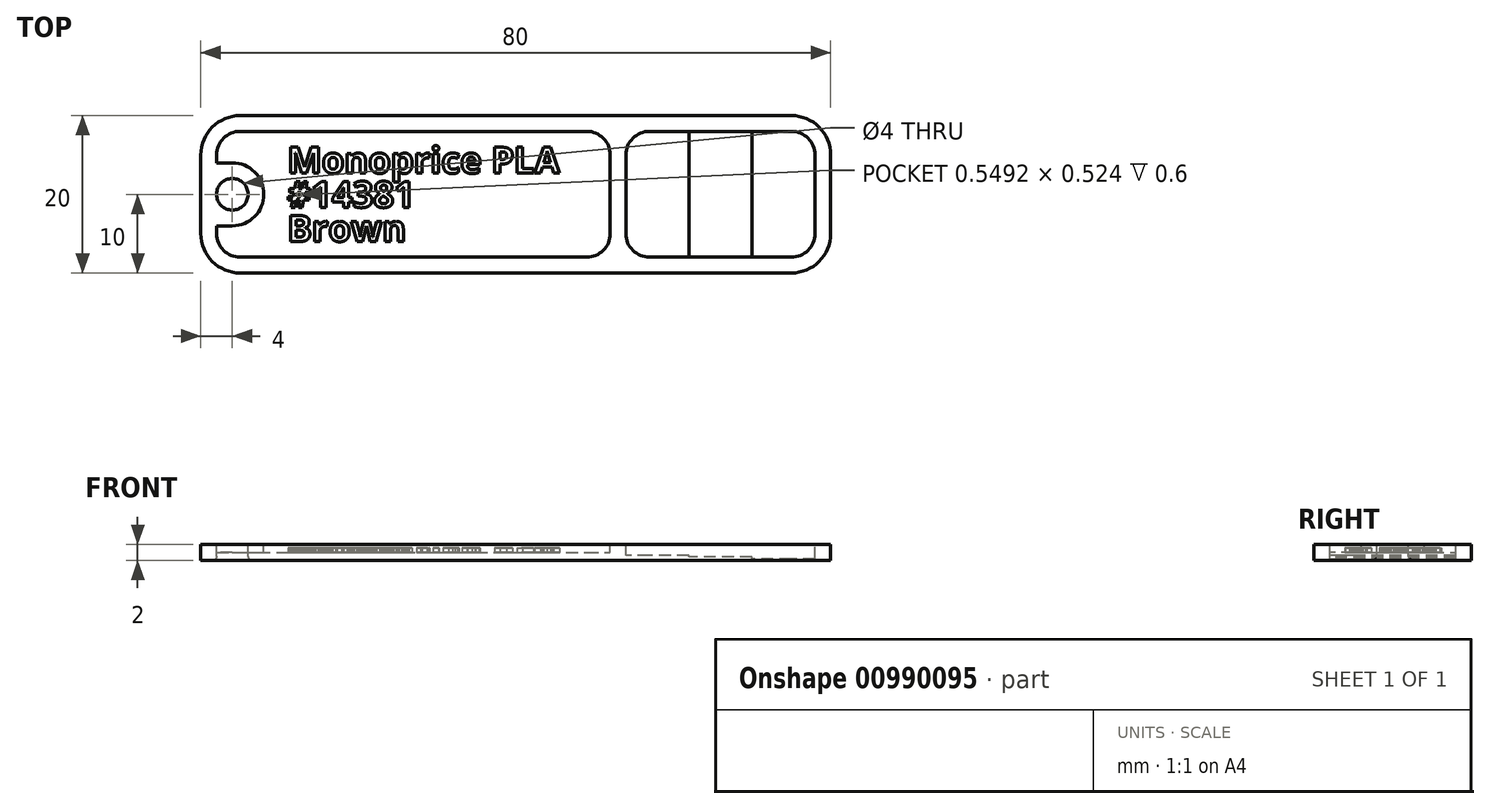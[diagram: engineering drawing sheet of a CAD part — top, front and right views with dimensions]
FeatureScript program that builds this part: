
annotation { "Feature Type Name" : "Feature", "Feature Type Description" : "" }
export const myFeature = defineFeature(function(context is Context, id is Id, definition is map)
    precondition{}
    {
        {
            var Q0;
            Q0=qCreatedBy(makeId("Top.planeOp"),FACE);
            var sketch = newSketch(context, id + "F0", { "sketchPlane" : qUnion([Q0])});
            skLineSegment(sketch, "E0.bottom", {"start": v(35, 10) * mm, "end": v(-35, 10) * mm});
            skLineSegment(sketch, "E0.top", {"start": v(35, -10) * mm, "end": v(-35, -10) * mm});
            skLineSegment(sketch, "E0.left", {"start": v(40, 5) * mm, "end": v(40, -5) * mm});
            skLineSegment(sketch, "E0.right", {"start": v(-40, 5) * mm, "end": v(-40, -5) * mm});
            skPoint(sketch, "E0.middle", {"position": v(0, 0) * mm});
            skPoint(sketch, "E1.visualSharp", {"position": v(-40, 10) * mm});
            skArc(sketch, "E1.filletArc", {"start": v(-35, 10) * mm, "mid": v(-38.54, 8.54) * mm, "end": v(-40, 5) * mm});
            skPoint(sketch, "E2.visualSharp", {"position": v(40, 10) * mm});
            skArc(sketch, "E2.filletArc", {"start": v(40, 5) * mm, "mid": v(38.54, 8.54) * mm, "end": v(35, 10) * mm});
            skPoint(sketch, "E3.visualSharp", {"position": v(40, -10) * mm});
            skArc(sketch, "E3.filletArc", {"start": v(35, -10) * mm, "mid": v(38.54, -8.54) * mm, "end": v(40, -5) * mm});
            skPoint(sketch, "E4.visualSharp", {"position": v(-40, -10) * mm});
            skArc(sketch, "E4.filletArc", {"start": v(-40, -5) * mm, "mid": v(-38.54, -8.54) * mm, "end": v(-35, -10) * mm});
            skSolve(sketch);
        }
        {
            var Q0;
            Q0=qSketchRegion(id+"F0",true);
            extrude(context, id + "F1", {"entities" : qUnion([Q0]), "offsetDistance" : 25 * mm, "depth" : 2 * mm});
        }
        {
            var Q0;
            Q0=makeQuery(id+"F1.opExtrude","CAP_FACE",FACE,{"disambiguationData":[OSD([sQuery(id+"F0.wireOp",EDGE,"E0.bottom"),sQuery(id+"F0.wireOp",EDGE,"E0.top"),sQuery(id+"F0.wireOp",EDGE,"E0.left"),sQuery(id+"F0.wireOp",EDGE,"E0.right"),sQuery(id+"F0.wireOp",EDGE,"E1.filletArc"),sQuery(id+"F0.wireOp",EDGE,"E2.filletArc"),sQuery(id+"F0.wireOp",EDGE,"E3.filletArc"),sQuery(id+"F0.wireOp",EDGE,"E4.filletArc")])],"isStart":false});
            var sketch = newSketch(context, id + "F2", { "sketchPlane" : qUnion([Q0])});
            skLineSegment(sketch, "E5.0", {"start": v(38, -5) * mm, "end": v(38, 5) * mm});
            skArc(sketch, "E5.1", {"start": v(35, -8) * mm, "mid": v(37.12, -7.12) * mm, "end": v(38, -5) * mm});
            skArc(sketch, "E5.2", {"start": v(38, 5) * mm, "mid": v(37.12, 7.12) * mm, "end": v(35, 8) * mm});
            skLineSegment(sketch, "E5.3", {"start": v(-35, -8) * mm, "end": v(9, -8) * mm});
            skLineSegment(sketch, "E5.4", {"start": v(35, 8) * mm, "end": v(17, 8) * mm});
            skArc(sketch, "E5.5", {"start": v(-35, 8) * mm, "mid": v(-37.12, 7.12) * mm, "end": v(-38, 5) * mm});
            skArc(sketch, "E5.7", {"start": v(-38, -5) * mm, "mid": v(-37.12, -7.12) * mm, "end": v(-35, -8) * mm});
            skCircle(sketch, "E6", {"center": v(-36, 0) * mm, "radius": 2 * mm, "construction": true});
            skArc(sketch, "E7.0", {"start": v(-36, -4) * mm, "mid": v(-32, 0) * mm, "end": v(-36, 4) * mm});
            skLineSegment(sketch, "E8", {"start": v(-38, -5) * mm, "end": v(-38, -4) * mm});
            skLineSegment(sketch, "E9", {"start": v(-36, 4) * mm, "end": v(-38, 4) * mm});
            skLineSegment(sketch, "E10", {"start": v(-36, -4) * mm, "end": v(-38, -4) * mm});
            skLineSegment(sketch, "E11.trimOffspring", {"start": v(-38, 4) * mm, "end": v(-38, 5) * mm});
            skArc(sketch, "E12", {"start": v(17, 8) * mm, "mid": v(14.88, 7.12) * mm, "end": v(14, 5) * mm});
            skArc(sketch, "E13", {"start": v(14, -5) * mm, "mid": v(14.88, -7.12) * mm, "end": v(17, -8) * mm});
            skLineSegment(sketch, "E14", {"start": v(14, -5) * mm, "end": v(14, 5) * mm});
            skArc(sketch, "E15", {"start": v(12, 5) * mm, "mid": v(11.12, 7.12) * mm, "end": v(9, 8) * mm});
            skArc(sketch, "E16", {"start": v(12, -5) * mm, "mid": v(11.12, -7.12) * mm, "end": v(9, -8) * mm});
            skLineSegment(sketch, "E17", {"start": v(12, -5) * mm, "end": v(12, 5) * mm});
            skLineSegment(sketch, "E18.trimOffspring", {"start": v(9, 8) * mm, "end": v(-35, 8) * mm});
            skLineSegment(sketch, "E19.trimOffspring", {"start": v(17, -8) * mm, "end": v(35, -8) * mm});
            skSolve(sketch);
        }
        {
            var Q0;
            Q0=qSketchRegion(id+"F2",true);
            extrude(context, id + "F3", {"entities" : qUnion([Q0]), "operationType" : NewBodyOperationType.REMOVE, "oppositeDirection" : true, "offsetDistance" : 25 * mm, "depth" : 1 * mm});
        }
        {
            var Q0;
            Q0=makeQuery(id+"F1.opExtrude","CAP_FACE",FACE,{"disambiguationData":[OSD([sQuery(id+"F0.wireOp",EDGE,"E0.bottom"),sQuery(id+"F0.wireOp",EDGE,"E0.top"),sQuery(id+"F0.wireOp",EDGE,"E0.left"),sQuery(id+"F0.wireOp",EDGE,"E0.right"),sQuery(id+"F0.wireOp",EDGE,"E1.filletArc"),sQuery(id+"F0.wireOp",EDGE,"E2.filletArc"),sQuery(id+"F0.wireOp",EDGE,"E3.filletArc"),sQuery(id+"F0.wireOp",EDGE,"E4.filletArc")])],"isStart":false});
            var sketch = newSketch(context, id + "F4", { "sketchPlane" : qUnion([Q0])});
            skCircle(sketch, "E20.0", {"center": v(-36, 0) * mm, "radius": 2 * mm});
            skSolve(sketch);
        }
        {
            var Q0;
            Q0=qSketchRegion(id+"F4",true);
            extrude(context, id + "F5", {"entities" : qUnion([Q0]), "operationType" : NewBodyOperationType.REMOVE, "endBound" : BoundingType.THROUGH_ALL, "oppositeDirection" : true, "depth" : 25 * mm});
        }
        {
            var Q0;
            Q0=makeQuery(id+"F5.boolean.opBoolean","COPY",EDGE,{"derivedFrom":makeQuery(id+"F5.opExtrude","CAP_EDGE",EDGE,{"disambiguationData":[OSD([sQuery(id+"F4.wireOp",EDGE,"E20.0")])],"isStart":true})});
            var Q1;
            Q1=makeQuery(id+"F5.boolean.opBoolean","INTERSECT",EDGE,{"derivedFrom":[makeQuery(id+"F1.opExtrude","CAP_FACE",FACE,{"disambiguationData":[OSD([sQuery(id+"F0.wireOp",EDGE,"E0.bottom"),sQuery(id+"F0.wireOp",EDGE,"E0.top"),sQuery(id+"F0.wireOp",EDGE,"E0.left"),sQuery(id+"F0.wireOp",EDGE,"E0.right"),sQuery(id+"F0.wireOp",EDGE,"E1.filletArc"),sQuery(id+"F0.wireOp",EDGE,"E2.filletArc"),sQuery(id+"F0.wireOp",EDGE,"E3.filletArc"),sQuery(id+"F0.wireOp",EDGE,"E4.filletArc")])],"isStart":true}),makeQuery(id+"F5.opExtrude","SWEPT_FACE",FACE,{"disambiguationData":[OSD([sQuery(id+"F4.wireOp",EDGE,"E20.0")])]})]});
            fillet(context, id + "F6", {"entities" : qUnion([Q0, Q1]), "radius" : .5 * mm, "tangentPropagation" : true, "allowEdgeOverflow" : false});
        }
        {
            var Q0;
            Q0=makeQuery(id+"F3.boolean.opBoolean","COPY",FACE,{"derivedFrom":makeQuery(id+"F3.opExtrude","CAP_FACE",FACE,{"disambiguationData":[OSD([sQuery(id+"F2.wireOp",EDGE,"E5.0"),sQuery(id+"F2.wireOp",EDGE,"E5.1"),sQuery(id+"F2.wireOp",EDGE,"E5.2"),sQuery(id+"F2.wireOp",EDGE,"E5.4"),sQuery(id+"F2.wireOp",EDGE,"E12"),sQuery(id+"F2.wireOp",EDGE,"E13"),sQuery(id+"F2.wireOp",EDGE,"E14"),sQuery(id+"F2.wireOp",EDGE,"E19.trimOffspring")])],"isStart":false})});
            extrude(context, id + "F7", {"entities" : qUnion([Q0]), "operationType" : NewBodyOperationType.REMOVE, "oppositeDirection" : true, "offsetDistance" : 25 * mm, "depth" : 0.4 * mm});
        }
        {
            var Q0;
            Q0=makeQuery(id+"F7.boolean.opBoolean","COPY",FACE,{"derivedFrom":makeQuery(id+"F7.opExtrude","CAP_FACE",FACE,{"disambiguationData":[OSD([sQuery(id+"F2.wireOp",EDGE,"E5.0"),sQuery(id+"F2.wireOp",EDGE,"E5.1"),sQuery(id+"F2.wireOp",EDGE,"E5.2"),sQuery(id+"F2.wireOp",EDGE,"E5.4"),sQuery(id+"F2.wireOp",EDGE,"E12"),sQuery(id+"F2.wireOp",EDGE,"E13"),sQuery(id+"F2.wireOp",EDGE,"E14"),sQuery(id+"F2.wireOp",EDGE,"E19.trimOffspring")])],"isStart":false})});
            var sketch = newSketch(context, id + "F8", { "sketchPlane" : qUnion([Q0])});
            skArc(sketch, "E21.0.0", {"start": v(35, -8) * mm, "mid": v(37.12, -7.12) * mm, "end": v(38, -5) * mm});
            skLineSegment(sketch, "E21.0.1", {"start": v(38, -5) * mm, "end": v(38, 5) * mm});
            skArc(sketch, "E21.0.2", {"start": v(38, 5) * mm, "mid": v(37.12, 7.12) * mm, "end": v(35, 8) * mm});
            skLineSegment(sketch, "E21.0.3", {"start": v(35, 8) * mm, "end": v(22, 8) * mm});
            skLineSegment(sketch, "E21.0.7", {"start": v(22, -8) * mm, "end": v(35, -8) * mm});
            skLineSegment(sketch, "E22", {"start": v(22, 8) * mm, "end": v(22, -8) * mm});
            skPoint(sketch, "E21.0.4.start.orphan", {"position": v(17, 8) * mm});
            skPoint(sketch, "E21.0.5.start.orphan", {"position": v(14, 5) * mm});
            skPoint(sketch, "E21.0.6.start.orphan", {"position": v(14, -5) * mm});
            skPoint(sketch, "E23.orphan", {"position": v(17, -8) * mm});
            skSolve(sketch);
        }
        {
            var Q0;
            Q0=qSketchRegion(id+"F8",true);
            extrude(context, id + "F9", {"entities" : qUnion([Q0]), "operationType" : NewBodyOperationType.REMOVE, "oppositeDirection" : true, "offsetDistance" : 25 * mm, "depth" : 0.2 * mm});
        }
        {
            var Q0;
            Q0=makeQuery(id+"F9.boolean.opBoolean","COPY",FACE,{"derivedFrom":makeQuery(id+"F9.opExtrude","CAP_FACE",FACE,{"disambiguationData":[OSD([sQuery(id+"F8.wireOp",EDGE,"E21.0.0"),sQuery(id+"F8.wireOp",EDGE,"E21.0.1"),sQuery(id+"F8.wireOp",EDGE,"E21.0.2"),sQuery(id+"F8.wireOp",EDGE,"E21.0.3"),sQuery(id+"F8.wireOp",EDGE,"E21.0.7"),sQuery(id+"F8.wireOp",EDGE,"E22")])],"isStart":false})});
            var sketch = newSketch(context, id + "F10", { "sketchPlane" : qUnion([Q0])});
            skLineSegment(sketch, "E24.0.0", {"start": v(35, 8) * mm, "end": v(30, 8) * mm});
            skLineSegment(sketch, "E24.0.2", {"start": v(30, -8) * mm, "end": v(35, -8) * mm});
            skArc(sketch, "E24.0.3", {"start": v(35, -8) * mm, "mid": v(37.12, -7.12) * mm, "end": v(38, -5) * mm});
            skLineSegment(sketch, "E24.0.4", {"start": v(38, -5) * mm, "end": v(38, 5) * mm});
            skArc(sketch, "E24.0.5", {"start": v(38, 5) * mm, "mid": v(37.12, 7.12) * mm, "end": v(35, 8) * mm});
            skLineSegment(sketch, "E25", {"start": v(30, 8) * mm, "end": v(30, -8) * mm});
            skPoint(sketch, "E24.0.1.end.orphan", {"position": v(22, -8) * mm});
            skPoint(sketch, "E26.orphan", {"position": v(22, 8) * mm});
            skSolve(sketch);
        }
        {
            var Q0;
            Q0=makeQuery(id+"F10.imprint","IMPRINT",FACE,{"disambiguationData":[TD([[makeQuery(id+"F10.imprint","IMPRINT",EDGE,{"derivedFrom":sQuery(id+"F10.wireOp",EDGE,"E24.0.0")}),1.0]])]});
            extrude(context, id + "F11", {"entities" : qUnion([Q0]), "operationType" : NewBodyOperationType.REMOVE, "oppositeDirection" : true, "offsetDistance" : 25 * mm, "depth" : 0.2 * mm});
        }
        {
            var Q0;
            Q0=makeQuery(id+"F3.boolean.opBoolean","COPY",FACE,{"derivedFrom":makeQuery(id+"F3.opExtrude","CAP_FACE",FACE,{"disambiguationData":[OSD([sQuery(id+"F2.wireOp",EDGE,"E5.3"),sQuery(id+"F2.wireOp",EDGE,"E5.5"),sQuery(id+"F2.wireOp",EDGE,"E5.7"),sQuery(id+"F2.wireOp",EDGE,"E7.0"),sQuery(id+"F2.wireOp",EDGE,"E8"),sQuery(id+"F2.wireOp",EDGE,"E9"),sQuery(id+"F2.wireOp",EDGE,"E10"),sQuery(id+"F2.wireOp",EDGE,"E11.trimOffspring"),sQuery(id+"F2.wireOp",EDGE,"E15"),sQuery(id+"F2.wireOp",EDGE,"E16"),sQuery(id+"F2.wireOp",EDGE,"E17"),sQuery(id+"F2.wireOp",EDGE,"E18.trimOffspring")])],"isStart":false})});
            var sketch = newSketch(context, id + "F12", { "sketchPlane" : qUnion([Q0])});
            skText(sketch, "E27", { "text": "Monoprice PLA", "fontName": "OpenSans-Bold.ttf"});
            skText(sketch, "E28", { "text": "#14381", "fontName": "OpenSans-Bold.ttf"});
            skText(sketch, "E29", { "text": "Brown", "fontName": "OpenSans-Bold.ttf"});
            skLineSegment(sketch, "E30", {"start": v(-27.83, 1.67) * mm, "end": v(-27.83, 2.67) * mm, "construction": true});
            skLineSegment(sketch, "E31", {"start": v(-26.66, -2.67) * mm, "end": v(-26.66, -1.67) * mm, "construction": true});
            skLineSegment(sketch, "E32.bottom", {"start": v(-31, 7) * mm, "end": v(10, 7) * mm, "construction": true});
            skLineSegment(sketch, "E32.top", {"start": v(-31, -7) * mm, "end": v(10, -7) * mm, "construction": true});
            skLineSegment(sketch, "E32.left", {"start": v(-31, 7) * mm, "end": v(-31, -7) * mm, "construction": true});
            skLineSegment(sketch, "E32.right", {"start": v(10, 7) * mm, "end": v(10, -7) * mm, "construction": true});
            skLineSegment(sketch, "E33", {"start": v(-13.47, 7) * mm, "end": v(-13.47, 8) * mm, "construction": true});
            skLineSegment(sketch, "E34", {"start": v(-13.67, -7) * mm, "end": v(-13.67, -8) * mm, "construction": true});
            skLineSegment(sketch, "E35", {"start": v(-32, 0) * mm, "end": v(-31, 0) * mm, "construction": true});
            skPoint(sketch, "E35.startSnap0", {"position": v(-31, 0) * mm});
            skLineSegment(sketch, "E36", {"start": v(-29, 4.33) * mm, "end": v(-31, 4.33) * mm, "construction": true});
            skLineSegment(sketch, "E37", {"start": v(10, 1.23) * mm, "end": v(12, 1.23) * mm, "construction": true});
            skLineSegment(sketch, "E38", {"start": v(-29, -0.54) * mm, "end": v(-31, -0.54) * mm, "construction": true});
            skLineSegment(sketch, "E39", {"start": v(-29, -4.33) * mm, "end": v(-31, -4.33) * mm, "construction": true});
            skLineSegment(sketch, "E40", {"start": v(-25.76, 6) * mm, "end": v(-25.76, 7) * mm, "construction": true});
            skLineSegment(sketch, "E41", {"start": v(-26.93, -6) * mm, "end": v(-26.93, -7) * mm, "construction": true});
            const initialGuessF12  = {"E27": [-0.029, 0.00267, 1, 0, 0.00333], "E28": [-0.029, -0.00167, 1, 0, 0.00333], "E29": [-0.029, -0.006, 1, 0, 0.00333]};
            skSetInitialGuess(sketch, initialGuessF12);
            skSolve(sketch);
        }
        {
            var Q0;
            Q0=qSketchRegion(id+"F12",true);
            extrude(context, id + "F13", {"entities" : qUnion([Q0]), "operationType" : NewBodyOperationType.ADD, "depth" : 0.6 * mm, "offsetDistance" : 25 * mm});
        }
    });
